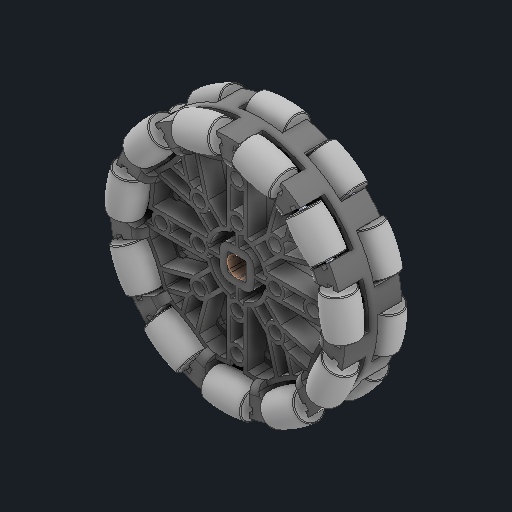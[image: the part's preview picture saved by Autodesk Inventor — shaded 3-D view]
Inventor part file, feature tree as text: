
AUTODESK INVENTOR PART (.ipt)
format: ipt  version: 2024 (Build 280153000, 153)  size: 3,344,384 bytes
history: native  units: in
note: dims shown in document units (in); Inventor stores cm internally (conversion verified against a paired STEP export)
features: other x49, sketch x1
ambient origin geometry x8: Origin, YZ Plane, XZ Plane, XY Plane, X Axis, Y Axis, Z Axis, Center Point
bodies: Solid1 (feature_tree), Solid2 (feature_tree), Solid3 (feature_tree), Solid4 (feature_tree), Solid5 (feature_tree), Solid6 (feature_tree), Solid7 (feature_tree), Solid8 (feature_tree), Solid9 (feature_tree), Solid10 (feature_tree), Solid11 (feature_tree), Solid12 (feature_tree), Solid13 (feature_tree), Solid14 (feature_tree), Solid15 (feature_tree), Solid16 (feature_tree), Solid17 (feature_tree), Solid18 (feature_tree), Solid19 (feature_tree), Solid20 (feature_tree), Solid21 (feature_tree), Solid22 (feature_tree), Solid23 (feature_tree), Solid24 (feature_tree), Solid25 (feature_tree), Solid26 (feature_tree), Solid27 (feature_tree), Solid28 (feature_tree), Solid29 (feature_tree), Solid30 (feature_tree), Solid31 (feature_tree), Solid32 (feature_tree), Solid33 (feature_tree), Solid34 (feature_tree), Solid35 (feature_tree), Solid36 (feature_tree), Solid37 (feature_tree), Solid38 (feature_tree), Solid39 (feature_tree), Solid40 (feature_tree), Solid41 (feature_tree), Solid42 (feature_tree), Solid43 (feature_tree), Solid44 (feature_tree), Solid45 (feature_tree)
feature tree (50):
  other  "3.25 Omni Antistatic.ipt"
  other  "Solid1::3.25 Omni Antistatic.ipt"
  other  "Solid2::3.25 Omni Antistatic.ipt"
  other  "Solid3::3.25 Omni Antistatic.ipt"
  other  "Solid4::3.25 Omni Antistatic.ipt"
  other  "Solid5::3.25 Omni Antistatic.ipt"
  other  "Solid6::3.25 Omni Antistatic.ipt"
  other  "Solid7::3.25 Omni Antistatic.ipt"
  other  "Solid8::3.25 Omni Antistatic.ipt"
  other  "Solid9::3.25 Omni Antistatic.ipt"
  other  "Solid10::3.25 Omni Antistatic.ipt"
  other  "Solid11::3.25 Omni Antistatic.ipt"
  other  "Solid12::3.25 Omni Antistatic.ipt"
  other  "Solid13::3.25 Omni Antistatic.ipt"
  other  "Solid14::3.25 Omni Antistatic.ipt"
  other  "Solid15::3.25 Omni Antistatic.ipt"
  other  "Solid16::3.25 Omni Antistatic.ipt"
  other  "Solid17::3.25 Omni Antistatic.ipt"
  other  "Solid18::3.25 Omni Antistatic.ipt"
  other  "Solid19::3.25 Omni Antistatic.ipt"
  other  "Solid20::3.25 Omni Antistatic.ipt"
  other  "Solid21::3.25 Omni Antistatic.ipt"
  other  "Solid22::3.25 Omni Antistatic.ipt"
  other  "Solid23::3.25 Omni Antistatic.ipt"
  other  "Solid24::3.25 Omni Antistatic.ipt"
  other  "Solid25::3.25 Omni Antistatic.ipt"
  other  "Solid26::3.25 Omni Antistatic.ipt"
  other  "Solid27::3.25 Omni Antistatic.ipt"
  other  "Solid28::3.25 Omni Antistatic.ipt"
  other  "Solid29::3.25 Omni Antistatic.ipt"
  other  "Solid30::3.25 Omni Antistatic.ipt"
  other  "Solid31::3.25 Omni Antistatic.ipt"
  other  "Solid32::3.25 Omni Antistatic.ipt"
  other  "Solid33::3.25 Omni Antistatic.ipt"
  other  "Solid34::3.25 Omni Antistatic.ipt"
  other  "Solid35::3.25 Omni Antistatic.ipt"
  other  "Solid36::3.25 Omni Antistatic.ipt"
  other  "Solid37::3.25 Omni Antistatic.ipt"
  other  "Solid38::3.25 Omni Antistatic.ipt"
  other  "Solid39::3.25 Omni Antistatic.ipt"
  other  "Solid40::3.25 Omni Antistatic.ipt"
  other  "Solid41::3.25 Omni Antistatic.ipt"
  other  "Solid42::3.25 Omni Antistatic.ipt"
  other  "Solid43::3.25 Omni Antistatic.ipt"
  other  "Solid44::3.25 Omni Antistatic.ipt"
  other  "Solid45::3.25 Omni Antistatic.ipt"
  other  "TaggingFeature1"
  sketch  "Sketch1"  dims[d0=0.3937in]
  other  "Srf1"
  other  "Srf1::Derived"
